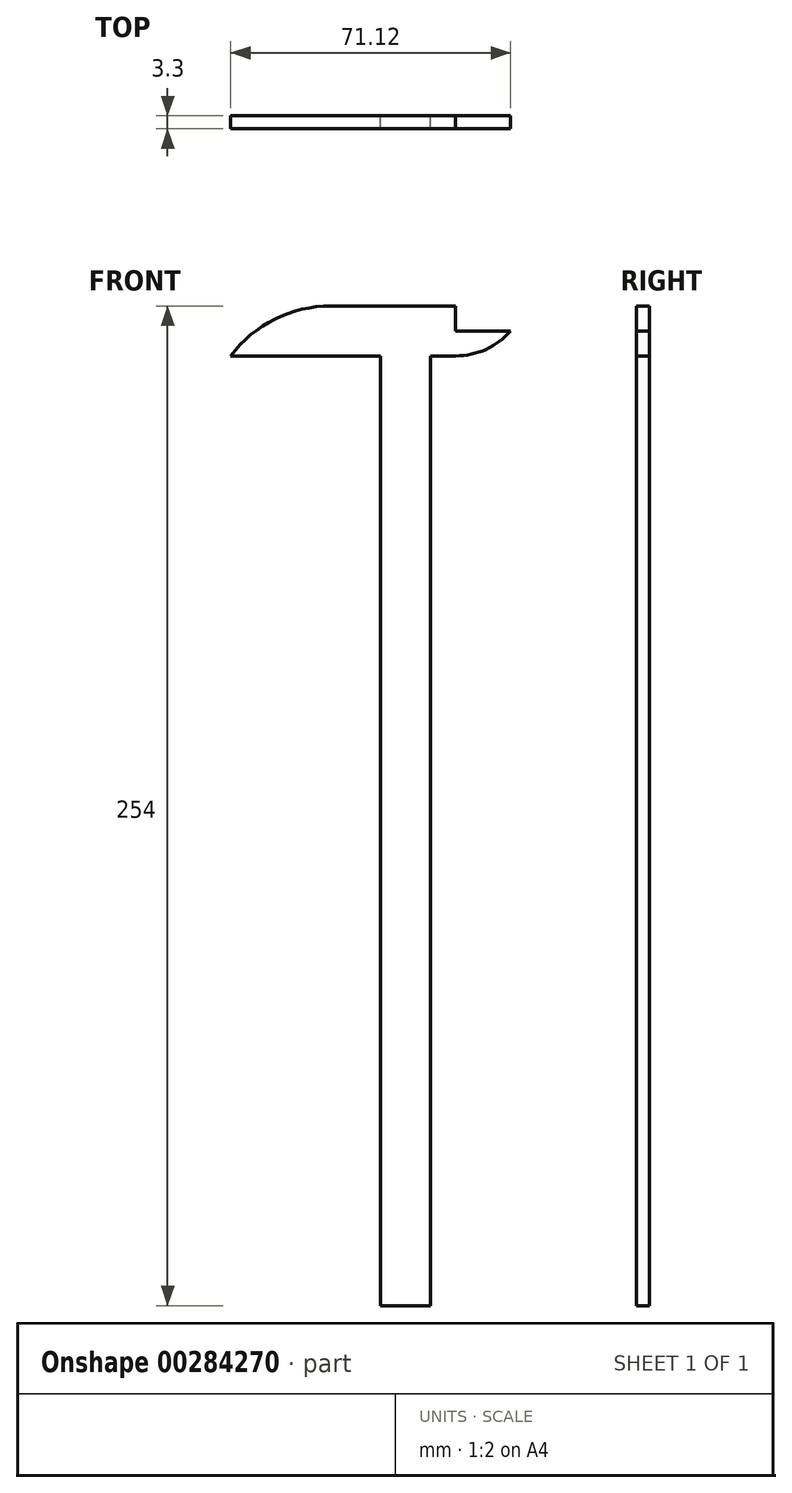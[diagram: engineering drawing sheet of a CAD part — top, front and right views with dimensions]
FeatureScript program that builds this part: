
annotation { "Feature Type Name" : "Feature", "Feature Type Description" : "" }
export const myFeature = defineFeature(function(context is Context, id is Id, definition is map)
    precondition{}
    {
        {
            var Q0;
            Q0=qCreatedBy(makeId("Front.planeOp"),FACE);
            var sketch = newSketch(context, id + "F0", { "sketchPlane" : qUnion([Q0])});
            skLineSegment(sketch, "E0.bottom", {"start": v(6.35, -120.65) * mm, "end": v(-6.35, -120.65) * mm});
            skLineSegment(sketch, "E0.top", {"start": v(6.35, 120.65) * mm, "end": v(-6.35, 120.65) * mm});
            skLineSegment(sketch, "E0.left", {"start": v(6.35, -120.65) * mm, "end": v(6.35, 120.65) * mm});
            skLineSegment(sketch, "E0.right", {"start": v(-6.35, -120.65) * mm, "end": v(-6.35, 120.65) * mm});
            skPoint(sketch, "E0.middle", {"position": v(0, 0) * mm});
            skLineSegment(sketch, "E1", {"start": v(6.35, 120.65) * mm, "end": v(12.7, 120.65) * mm});
            skLineSegment(sketch, "E2", {"start": v(12.7, 120.65) * mm, "end": v(12.7, 133.35) * mm});
            skLineSegment(sketch, "E3", {"start": v(12.7, 133.35) * mm, "end": v(-19.05, 133.35) * mm});
            skLineSegment(sketch, "E4", {"start": v(-6.35, 120.65) * mm, "end": v(-44.45, 120.65) * mm});
            skArc(sketch, "E5", {"start": v(-19.05, 133.35) * mm, "mid": v(-33.25, 130) * mm, "end": v(-44.45, 120.65) * mm});
            skLineSegment(sketch, "E6", {"start": v(12.7, 127) * mm, "end": v(26.67, 127) * mm});
            skArc(sketch, "E7", {"start": v(12.7, 120.65) * mm, "mid": v(20.37, 122.31) * mm, "end": v(26.67, 127) * mm});
            skLineSegment(sketch, "E8", {"start": v(-6.35, 120.65) * mm, "end": v(-6.35, 133.35) * mm});
            skLineSegment(sketch, "E9", {"start": v(6.35, 120.65) * mm, "end": v(6.35, 133.35) * mm});
            skSolve(sketch);
        }
        {
            var Q0;
            Q0 = qSketchRegion(id + "F0", true);
            extrude(context, id + "F1", {"entities" : qUnion([Q0]), "endBound" : BoundingType.SYMMETRIC, "depth" : 3.3 * mm});
        }
    });
